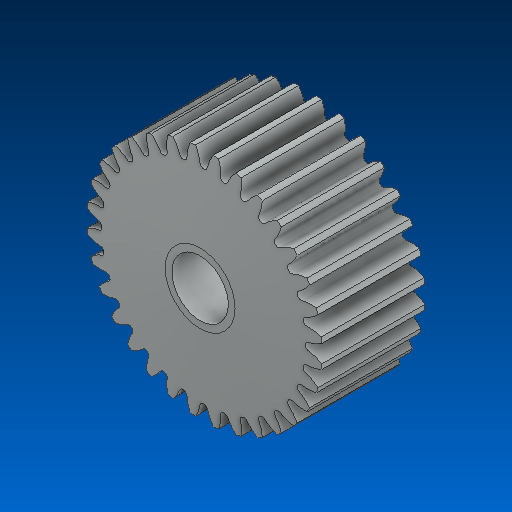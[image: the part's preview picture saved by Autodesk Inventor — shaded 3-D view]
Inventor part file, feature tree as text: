
AUTODESK INVENTOR PART (.ipt)
format: ipt  version: 2022.2 (Build 262287000, 287)  size: 514,048 bytes
history: native  units: in
note: dims shown in document units (in); Inventor stores cm internally (conversion verified against a paired STEP export)
features: mirror x1
ambient origin geometry x8: Origin, YZ Plane, XZ Plane, XY Plane, X Axis, Y Axis, Z Axis, Center Point
bodies: Solid1 (feature_tree)
feature tree (1):
  mirror  "Mirror1"
